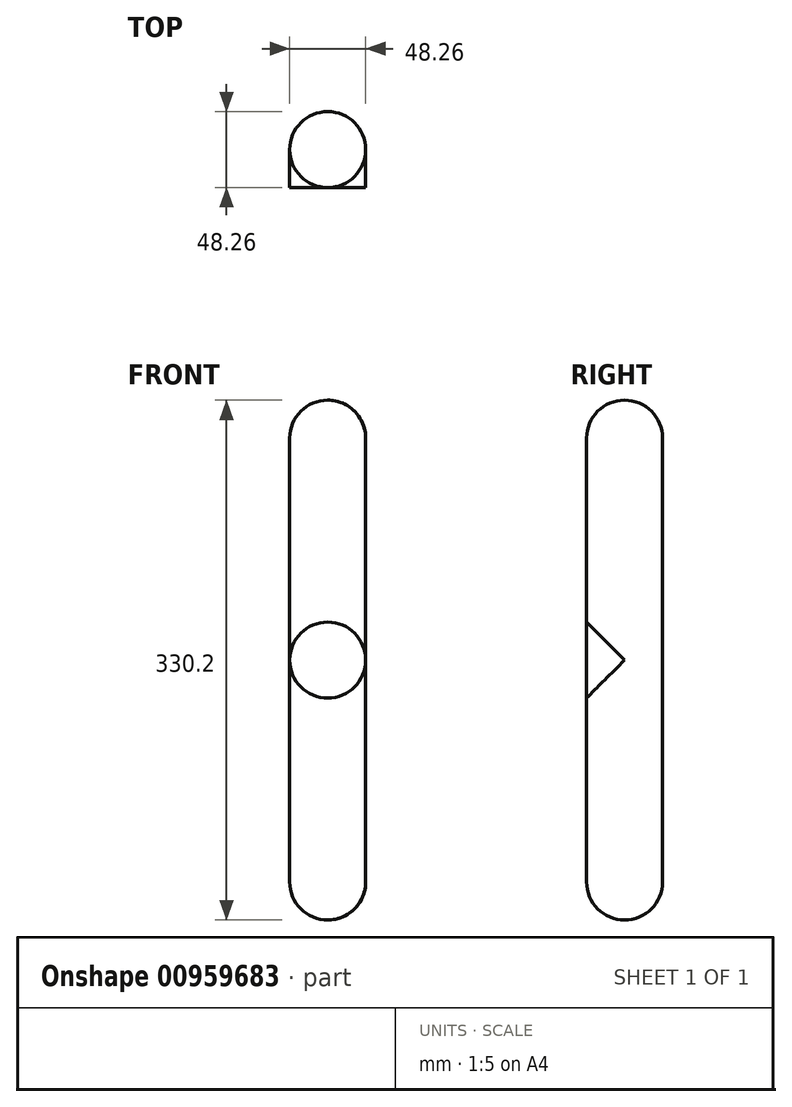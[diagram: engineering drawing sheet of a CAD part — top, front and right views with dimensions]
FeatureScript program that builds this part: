
annotation { "Feature Type Name" : "Feature", "Feature Type Description" : "" }
export const myFeature = defineFeature(function(context is Context, id is Id, definition is map)
    precondition{}
    {
        {
            var Q0;
            Q0=qCreatedBy(makeId("Top.planeOp"),FACE);
            var sketch = newSketch(context, id + "F0", { "sketchPlane" : qUnion([Q0])});
            skCircle(sketch, "E0", {"center": v(0, 0) * mm, "radius": 24.13 * mm});
            skSolve(sketch);
        }
        {
            var Q0;
            Q0=makeQuery(id+"F0.imprint","IMPRINT",FACE,{"disambiguationData":[TD([[makeQuery(id+"F0.imprint","IMPRINT",EDGE,{"derivedFrom":sQuery(id+"F0.wireOp",EDGE,"E0")}),1.0]])]});
            extrude(context, id + "F1", {"entities" : qUnion([Q0]), "depth" : 330.2 * mm, "offsetDistance" : 25.4 * mm});
        }
        {
            var Q0;
            Q0=makeQuery(id+"F1.opExtrude","CAP_EDGE",EDGE,{"disambiguationData":[OSD([sQuery(id+"F0.wireOp",EDGE,"E0")])],"isStart":false});
            fillet(context, id + "F2", {"entities" : qUnion([Q0]), "radius" : 24.13 * mm, "tangentPropagation" : true, "allowEdgeOverflow" : false});
        }
        {
            var Q0;
            Q0=makeQuery(id+"F1.opExtrude","CAP_EDGE",EDGE,{"disambiguationData":[OSD([sQuery(id+"F0.wireOp",EDGE,"E0")])],"isStart":true});
            fillet(context, id + "F3", {"entities" : qUnion([Q0]), "radius" : 24.13 * mm, "tangentPropagation" : true, "allowEdgeOverflow" : false});
        }
        {
            var Q0;
            Q0=qCreatedBy(makeId("Front.planeOp"),FACE);
            var sketch = newSketch(context, id + "F4", { "sketchPlane" : qUnion([Q0])});
            skCircle(sketch, "E1", {"center": v(0, 165.1) * mm, "radius": 24.13 * mm});
            skSolve(sketch);
        }
        {
            var Q0;
            Q0 = qSketchRegion(id + "F4", true);
            extrude(context, id + "F5", {"entities" : qUnion([Q0]), "operationType" : NewBodyOperationType.ADD, "depth" : 24.13 * mm, "offsetDistance" : 25.4 * mm});
        }
    });
